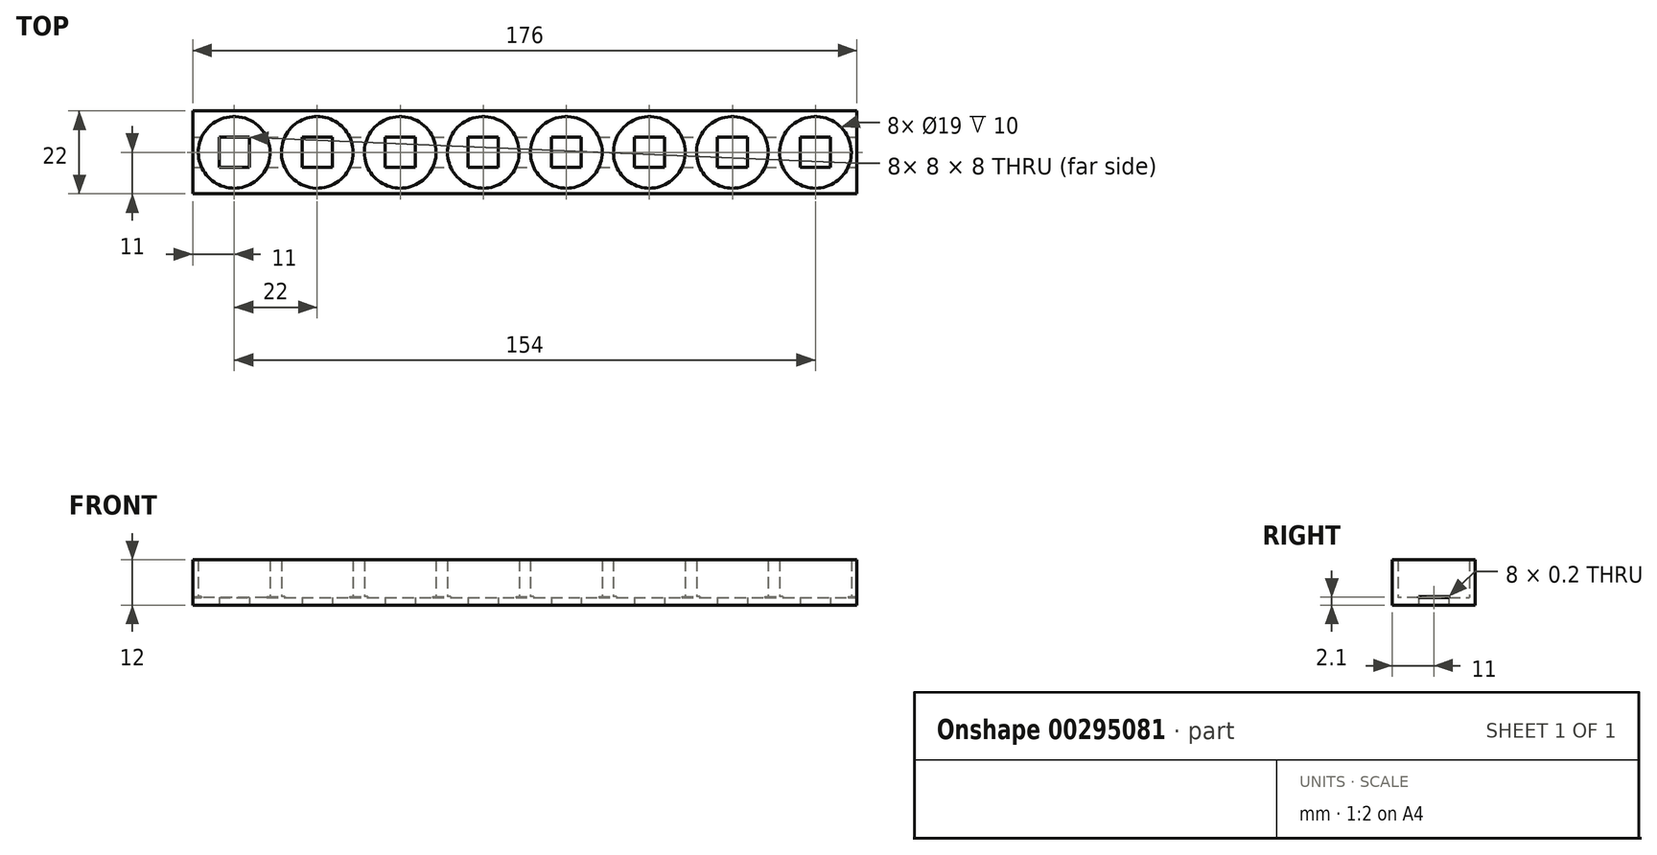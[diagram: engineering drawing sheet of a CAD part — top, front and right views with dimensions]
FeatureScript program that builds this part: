
annotation { "Feature Type Name" : "Feature", "Feature Type Description" : "" }
export const myFeature = defineFeature(function(context is Context, id is Id, definition is map)
    precondition{}
    {
        {
            var Q0;
            Q0=qCreatedBy(makeId("Top.planeOp"),FACE);
            var sketch = newSketch(context, id + "F0", { "sketchPlane" : qUnion([Q0])});
            skLineSegment(sketch, "E0.bottom", {"start": v(11, 11) * mm, "end": v(-11, 11) * mm});
            skLineSegment(sketch, "E0.top", {"start": v(11, -11) * mm, "end": v(-11, -11) * mm});
            skLineSegment(sketch, "E0.left", {"start": v(11, 11) * mm, "end": v(11, -11) * mm});
            skLineSegment(sketch, "E0.right", {"start": v(-11, 11) * mm, "end": v(-11, -11) * mm});
            skPoint(sketch, "E0.middle", {"position": v(0, 0) * mm});
            skLineSegment(sketch, "E1.bottom", {"start": v(-4, 4) * mm, "end": v(4, 4) * mm});
            skLineSegment(sketch, "E1.top", {"start": v(-4, -4) * mm, "end": v(4, -4) * mm});
            skLineSegment(sketch, "E1.left", {"start": v(-4, 4) * mm, "end": v(-4, -4) * mm});
            skLineSegment(sketch, "E1.right", {"start": v(4, 4) * mm, "end": v(4, -4) * mm});
            skLineSegment(sketch, "E2.1.0.0", {"start": v(26, 4) * mm, "end": v(26, -4) * mm});
            skLineSegment(sketch, "E2.1.0.1", {"start": v(33, -11) * mm, "end": v(11, -11) * mm});
            skLineSegment(sketch, "E2.1.0.2", {"start": v(33, 11) * mm, "end": v(11, 11) * mm});
            skLineSegment(sketch, "E2.1.0.3", {"start": v(18, 4) * mm, "end": v(18, -4) * mm});
            skLineSegment(sketch, "E2.1.0.5", {"start": v(18, 4) * mm, "end": v(26, 4) * mm});
            skLineSegment(sketch, "E2.1.0.6", {"start": v(18, -4) * mm, "end": v(26, -4) * mm});
            skLineSegment(sketch, "E2.1.0.7", {"start": v(33, 11) * mm, "end": v(33, -11) * mm});
            skPoint(sketch, "E2.1.0.8", {"position": v(22, 0) * mm});
            skPoint(sketch, "E2.1.0.9", {"position": v(22, 0) * mm});
            skLineSegment(sketch, "E2.2.0.0", {"start": v(48, 4) * mm, "end": v(48, -4) * mm});
            skLineSegment(sketch, "E2.2.0.1", {"start": v(55, -11) * mm, "end": v(33, -11) * mm});
            skLineSegment(sketch, "E2.2.0.2", {"start": v(55, 11) * mm, "end": v(33, 11) * mm});
            skLineSegment(sketch, "E2.2.0.3", {"start": v(40, 4) * mm, "end": v(40, -4) * mm});
            skLineSegment(sketch, "E2.2.0.4", {"start": v(33, 11) * mm, "end": v(33, -11) * mm});
            skLineSegment(sketch, "E2.2.0.5", {"start": v(40, 4) * mm, "end": v(48, 4) * mm});
            skLineSegment(sketch, "E2.2.0.6", {"start": v(40, -4) * mm, "end": v(48, -4) * mm});
            skLineSegment(sketch, "E2.2.0.7", {"start": v(55, 11) * mm, "end": v(55, -11) * mm});
            skPoint(sketch, "E2.2.0.8", {"position": v(44, 0) * mm});
            skPoint(sketch, "E2.2.0.9", {"position": v(44, 0) * mm});
            skLineSegment(sketch, "E2.3.0.0", {"start": v(70, 4) * mm, "end": v(70, -4) * mm});
            skLineSegment(sketch, "E2.3.0.1", {"start": v(77, -11) * mm, "end": v(55, -11) * mm});
            skLineSegment(sketch, "E2.3.0.2", {"start": v(77, 11) * mm, "end": v(55, 11) * mm});
            skLineSegment(sketch, "E2.3.0.3", {"start": v(62, 4) * mm, "end": v(62, -4) * mm});
            skLineSegment(sketch, "E2.3.0.4", {"start": v(55, 11) * mm, "end": v(55, -11) * mm});
            skLineSegment(sketch, "E2.3.0.5", {"start": v(62, 4) * mm, "end": v(70, 4) * mm});
            skLineSegment(sketch, "E2.3.0.6", {"start": v(62, -4) * mm, "end": v(70, -4) * mm});
            skLineSegment(sketch, "E2.3.0.7", {"start": v(77, 11) * mm, "end": v(77, -11) * mm});
            skPoint(sketch, "E2.3.0.8", {"position": v(66, 0) * mm});
            skPoint(sketch, "E2.3.0.9", {"position": v(66, 0) * mm});
            skLineSegment(sketch, "E2.4.0.0", {"start": v(92, 4) * mm, "end": v(92, -4) * mm});
            skLineSegment(sketch, "E2.4.0.1", {"start": v(99, -11) * mm, "end": v(77, -11) * mm});
            skLineSegment(sketch, "E2.4.0.2", {"start": v(99, 11) * mm, "end": v(77, 11) * mm});
            skLineSegment(sketch, "E2.4.0.3", {"start": v(84, 4) * mm, "end": v(84, -4) * mm});
            skLineSegment(sketch, "E2.4.0.4", {"start": v(77, 11) * mm, "end": v(77, -11) * mm});
            skLineSegment(sketch, "E2.4.0.5", {"start": v(84, 4) * mm, "end": v(92, 4) * mm});
            skLineSegment(sketch, "E2.4.0.6", {"start": v(84, -4) * mm, "end": v(92, -4) * mm});
            skLineSegment(sketch, "E2.4.0.7", {"start": v(99, 11) * mm, "end": v(99, -11) * mm});
            skPoint(sketch, "E2.4.0.8", {"position": v(88, 0) * mm});
            skPoint(sketch, "E2.4.0.9", {"position": v(88, 0) * mm});
            skLineSegment(sketch, "E2.5.0.0", {"start": v(114, 4) * mm, "end": v(114, -4) * mm});
            skLineSegment(sketch, "E2.5.0.1", {"start": v(121, -11) * mm, "end": v(99, -11) * mm});
            skLineSegment(sketch, "E2.5.0.2", {"start": v(121, 11) * mm, "end": v(99, 11) * mm});
            skLineSegment(sketch, "E2.5.0.3", {"start": v(106, 4) * mm, "end": v(106, -4) * mm});
            skLineSegment(sketch, "E2.5.0.4", {"start": v(99, 11) * mm, "end": v(99, -11) * mm});
            skLineSegment(sketch, "E2.5.0.5", {"start": v(106, 4) * mm, "end": v(114, 4) * mm});
            skLineSegment(sketch, "E2.5.0.6", {"start": v(106, -4) * mm, "end": v(114, -4) * mm});
            skLineSegment(sketch, "E2.5.0.7", {"start": v(121, 11) * mm, "end": v(121, -11) * mm});
            skPoint(sketch, "E2.5.0.8", {"position": v(110, 0) * mm});
            skPoint(sketch, "E2.5.0.9", {"position": v(110, 0) * mm});
            skLineSegment(sketch, "E2.6.0.0", {"start": v(136, 4) * mm, "end": v(136, -4) * mm});
            skLineSegment(sketch, "E2.6.0.1", {"start": v(143, -11) * mm, "end": v(121, -11) * mm});
            skLineSegment(sketch, "E2.6.0.2", {"start": v(143, 11) * mm, "end": v(121, 11) * mm});
            skLineSegment(sketch, "E2.6.0.3", {"start": v(128, 4) * mm, "end": v(128, -4) * mm});
            skLineSegment(sketch, "E2.6.0.4", {"start": v(121, 11) * mm, "end": v(121, -11) * mm});
            skLineSegment(sketch, "E2.6.0.5", {"start": v(128, 4) * mm, "end": v(136, 4) * mm});
            skLineSegment(sketch, "E2.6.0.6", {"start": v(128, -4) * mm, "end": v(136, -4) * mm});
            skLineSegment(sketch, "E2.6.0.7", {"start": v(143, 11) * mm, "end": v(143, -11) * mm});
            skPoint(sketch, "E2.6.0.8", {"position": v(132, 0) * mm});
            skPoint(sketch, "E2.6.0.9", {"position": v(132, 0) * mm});
            skLineSegment(sketch, "E2.7.0.0", {"start": v(158, 4) * mm, "end": v(158, -4) * mm});
            skLineSegment(sketch, "E2.7.0.1", {"start": v(165, -11) * mm, "end": v(143, -11) * mm});
            skLineSegment(sketch, "E2.7.0.2", {"start": v(165, 11) * mm, "end": v(143, 11) * mm});
            skLineSegment(sketch, "E2.7.0.3", {"start": v(150, 4) * mm, "end": v(150, -4) * mm});
            skLineSegment(sketch, "E2.7.0.4", {"start": v(143, 11) * mm, "end": v(143, -11) * mm});
            skLineSegment(sketch, "E2.7.0.5", {"start": v(150, 4) * mm, "end": v(158, 4) * mm});
            skLineSegment(sketch, "E2.7.0.6", {"start": v(150, -4) * mm, "end": v(158, -4) * mm});
            skLineSegment(sketch, "E2.7.0.7", {"start": v(165, 11) * mm, "end": v(165, -11) * mm});
            skPoint(sketch, "E2.7.0.8", {"position": v(154, 0) * mm});
            skPoint(sketch, "E2.7.0.9", {"position": v(154, 0) * mm});
            skLineSegment(sketch, "E2.direction1", {"start": v(-11, -11) * mm, "end": v(11, -11) * mm, "construction": true});
            skSolve(sketch);
        }
        {
            var Q0;
            Q0 = qSketchRegion(id + "F0", true);
            extrude(context, id + "F1", {"entities" : qUnion([Q0]), "depth" : 2 * mm});
        }
        {
            var Q0;
            Q0=makeQuery(id+"F1.opExtrude","CAP_FACE",FACE,{"disambiguationData":[OSD([sQuery(id+"F0.wireOp",EDGE,"E0.bottom"),sQuery(id+"F0.wireOp",EDGE,"E0.top"),sQuery(id+"F0.wireOp",EDGE,"E0.left"),sQuery(id+"F0.wireOp",EDGE,"E0.right"),sQuery(id+"F0.wireOp",EDGE,"E1.bottom"),sQuery(id+"F0.wireOp",EDGE,"E1.top"),sQuery(id+"F0.wireOp",EDGE,"E1.left"),sQuery(id+"F0.wireOp",EDGE,"E1.right")])],"isStart":false});
            var sketch = newSketch(context, id + "F2", { "sketchPlane" : qUnion([Q0])});
            skCircle(sketch, "E3", {"center": v(0, 0) * mm, "radius": 9.5 * mm});
            skCircle(sketch, "E4.1.0.0", {"center": v(22, 0) * mm, "radius": 9.5 * mm});
            skCircle(sketch, "E4.2.0.0", {"center": v(44, 0) * mm, "radius": 9.5 * mm});
            skCircle(sketch, "E4.3.0.0", {"center": v(66, 0) * mm, "radius": 9.5 * mm});
            skCircle(sketch, "E4.4.0.0", {"center": v(88, 0) * mm, "radius": 9.5 * mm});
            skCircle(sketch, "E4.5.0.0", {"center": v(110, 0) * mm, "radius": 9.5 * mm});
            skCircle(sketch, "E4.6.0.0", {"center": v(132, 0) * mm, "radius": 9.5 * mm});
            skCircle(sketch, "E4.7.0.0", {"center": v(154, 0) * mm, "radius": 9.5 * mm});
            skLineSegment(sketch, "E4.direction1", {"start": v(0, 0) * mm, "end": v(22, 0) * mm, "construction": true});
            skSolve(sketch);
        }
        {
            var Q0;
            Q0=makeQuery(id+"F2.imprint","IMPRINT",FACE,{"disambiguationData":[TD([[makeQuery(id+"F2.imprint","IMPRINT",EDGE,{"derivedFrom":sQuery(id+"F2.wireOp",EDGE,"E3")}),-1.0]])]});
            extrude(context, id + "F3", {"entities" : qUnion([Q0]), "operationType" : NewBodyOperationType.ADD, "depth" : 10 * mm});
        }
        {
            var Q0;
            {var subQ0=sQuery(id+"F0.wireOp",EDGE,"E2.7.0.7");Q0=makeQuery(id+"F3.boolean.opBoolean","MERGE",FACE,{"derivedFrom":[makeQuery(id+"F1.opExtrude","SWEPT_FACE",FACE,{"disambiguationData":[OSD([subQ0])]}),makeQuery(id+"F3.opExtrude","SWEPT_FACE",FACE,{"disambiguationData":[OSD([subQ0])]})]});}
            var sketch = newSketch(context, id + "F4", { "sketchPlane" : qUnion([Q0])});
            skLineSegment(sketch, "E5.bottom", {"start": v(-4, 2.2) * mm, "end": v(4, 2.2) * mm});
            skLineSegment(sketch, "E5.top", {"start": v(-4, 2) * mm, "end": v(4, 2) * mm});
            skLineSegment(sketch, "E5.left", {"start": v(-4, 2.2) * mm, "end": v(-4, 2) * mm});
            skLineSegment(sketch, "E5.right", {"start": v(4, 2.2) * mm, "end": v(4, 2) * mm});
            skSolve(sketch);
        }
        {
            var Q0;
            Q0=makeQuery(id+"F4.imprint","IMPRINT",FACE,{"disambiguationData":[TD([[makeQuery(id+"F4.imprint","IMPRINT",EDGE,{"derivedFrom":sQuery(id+"F4.wireOp",EDGE,"E5.bottom")}),-1.0]])]});
            extrude(context, id + "F5", {"entities" : qUnion([Q0]), "operationType" : NewBodyOperationType.REMOVE, "endBound" : BoundingType.THROUGH_ALL, "oppositeDirection" : true, "depth" : 25 * mm});
        }
    });
